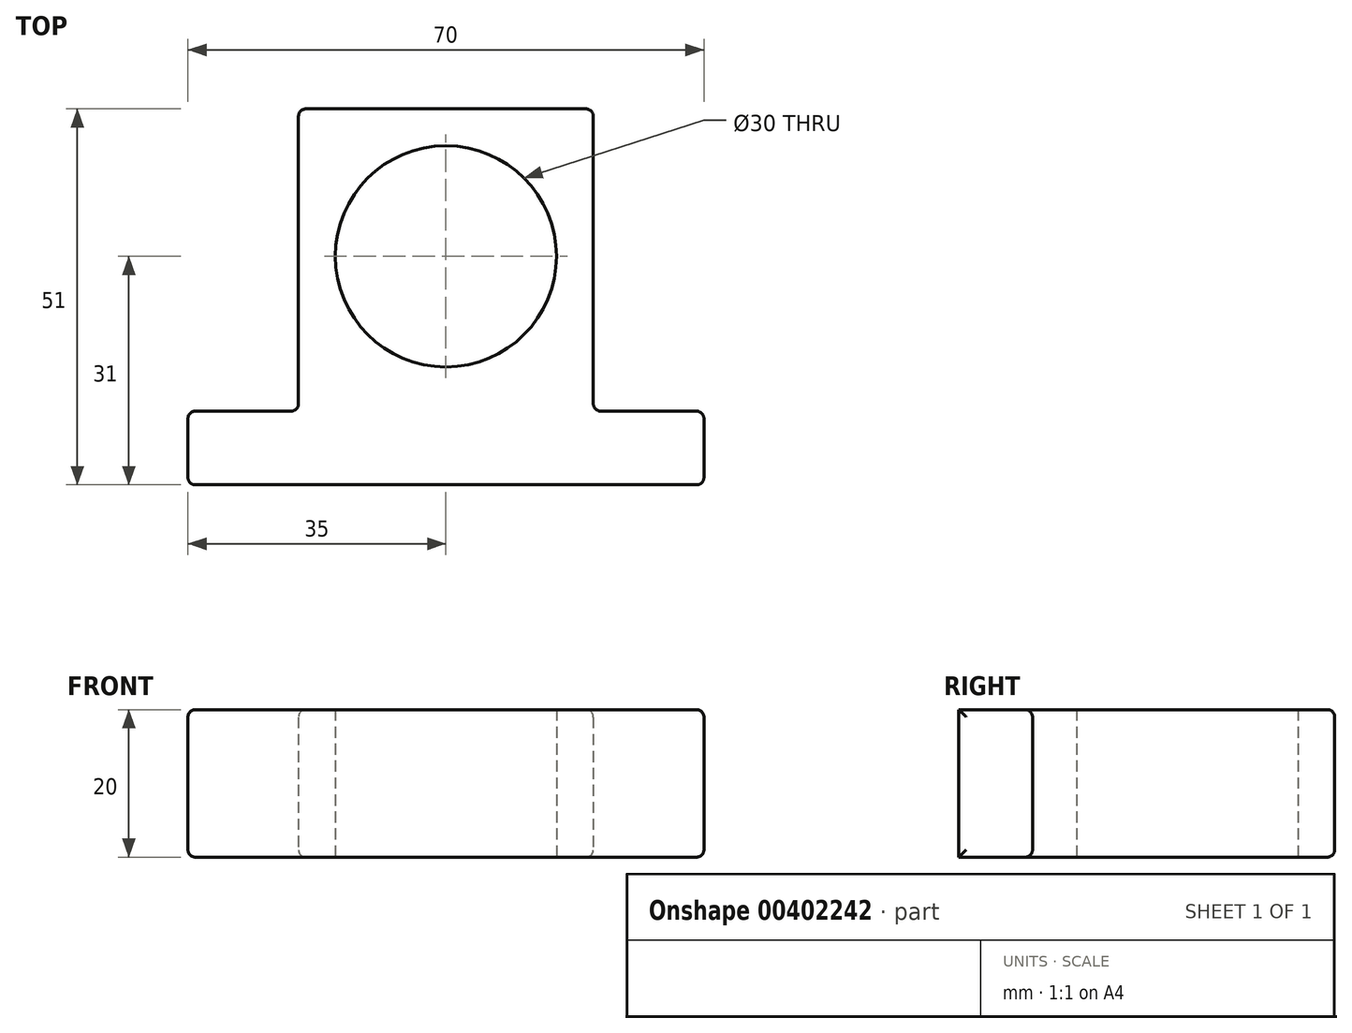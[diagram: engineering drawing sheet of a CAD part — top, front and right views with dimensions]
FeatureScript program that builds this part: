
annotation { "Feature Type Name" : "Feature", "Feature Type Description" : "" }
export const myFeature = defineFeature(function(context is Context, id is Id, definition is map)
    precondition{}
    {
        {
            var Q0;
            Q0=qCreatedBy(makeId("Top.planeOp"),FACE);
            var sketch = newSketch(context, id + "F0", { "sketchPlane" : qUnion([Q0])});
            skLineSegment(sketch, "E0.bottom", {"start": v(20, -25.5) * mm, "end": v(-20, -25.5) * mm});
            skLineSegment(sketch, "E0.top", {"start": v(20, 25.5) * mm, "end": v(-20, 25.5) * mm});
            skLineSegment(sketch, "E0.left", {"start": v(20, -25.5) * mm, "end": v(20, 25.5) * mm});
            skLineSegment(sketch, "E0.right", {"start": v(-20, -25.5) * mm, "end": v(-20, 25.5) * mm});
            skPoint(sketch, "E0.middle", {"position": v(0, 0) * mm});
            skLineSegment(sketch, "E1.bottom", {"start": v(20, -25.5) * mm, "end": v(35, -25.5) * mm});
            skLineSegment(sketch, "E1.top", {"start": v(20, -15.5) * mm, "end": v(35, -15.5) * mm});
            skLineSegment(sketch, "E1.left", {"start": v(20, -25.5) * mm, "end": v(20, -15.5) * mm});
            skLineSegment(sketch, "E1.right", {"start": v(35, -25.5) * mm, "end": v(35, -15.5) * mm});
            skLineSegment(sketch, "E2.bottom", {"start": v(-20, -25.5) * mm, "end": v(-35, -25.5) * mm});
            skLineSegment(sketch, "E2.top", {"start": v(-20, -15.5) * mm, "end": v(-35, -15.5) * mm});
            skLineSegment(sketch, "E2.left", {"start": v(-20, -25.5) * mm, "end": v(-20, -15.5) * mm});
            skLineSegment(sketch, "E2.right", {"start": v(-35, -25.5) * mm, "end": v(-35, -15.5) * mm});
            skCircle(sketch, "E3", {"center": v(0, 5.5) * mm, "radius": 15 * mm});
            skSolve(sketch);
        }
        {
            var Q0;
            Q0=makeQuery(id+"F0.imprint","IMPRINT",FACE,{"disambiguationData":[TD([[makeQuery(id+"F0.imprint","IMPRINT",EDGE,{"derivedFrom":sQuery(id+"F0.wireOp",EDGE,"E0.bottom")}),-1.0]])]});
            var Q1;
            Q1=makeQuery(id+"F0.imprint","IMPRINT",FACE,{"disambiguationData":[TD([[makeQuery(id+"F0.imprint","IMPRINT",EDGE,{"derivedFrom":sQuery(id+"F0.wireOp",EDGE,"E2.bottom")}),-1.0]])]});
            var Q2;
            Q2=makeQuery(id+"F0.imprint","IMPRINT",FACE,{"disambiguationData":[TD([[makeQuery(id+"F0.imprint","IMPRINT",EDGE,{"derivedFrom":sQuery(id+"F0.wireOp",EDGE,"E1.bottom")}),1.0]])]});
            extrude(context, id + "F1", {"entities" : qUnion([Q0, Q1, Q2]), "depth" : 20 * mm});
        }
        {
            var Q0;
            Q0=makeQuery(id+"F1.opExtrude","SWEPT_FACE",FACE,{"disambiguationData":[OSD([sQuery(id+"F0.wireOp",EDGE,"E0.right")])]});
            var Q1;
            Q1=makeQuery(id+"F1.opExtrude","SWEPT_FACE",FACE,{"disambiguationData":[OSD([sQuery(id+"F0.wireOp",EDGE,"E0.top")])]});
            var Q2;
            Q2=makeQuery(id+"F1.opExtrude","SWEPT_FACE",FACE,{"disambiguationData":[OSD([sQuery(id+"F0.wireOp",EDGE,"E0.left")])]});
            fillet(context, id + "F2", {"entities" : qUnion([Q0, Q1, Q2]), "radius" : 1 * mm, "tangentPropagation" : true, "allowEdgeOverflow" : false});
        }
        {
            var Q0;
            Q0=makeQuery(id+"F1.opExtrude","SWEPT_FACE",FACE,{"disambiguationData":[OSD([sQuery(id+"F0.wireOp",EDGE,"E1.top")])]});
            var Q1;
            Q1=makeQuery(id+"F1.opExtrude","SWEPT_FACE",FACE,{"disambiguationData":[OSD([sQuery(id+"F0.wireOp",EDGE,"E1.right")])]});
            var Q2;
            Q2=makeQuery(id+"F1.opExtrude","SWEPT_FACE",FACE,{"disambiguationData":[OSD([sQuery(id+"F0.wireOp",EDGE,"E2.top")])]});
            var Q3;
            Q3=makeQuery(id+"F1.opExtrude","SWEPT_FACE",FACE,{"disambiguationData":[OSD([sQuery(id+"F0.wireOp",EDGE,"E2.right")])]});
            fillet(context, id + "F3", {"entities" : qUnion([Q0, Q1, Q2, Q3]), "radius" : 1 * mm, "tangentPropagation" : true, "allowEdgeOverflow" : false});
        }
    });
